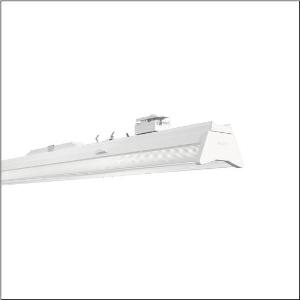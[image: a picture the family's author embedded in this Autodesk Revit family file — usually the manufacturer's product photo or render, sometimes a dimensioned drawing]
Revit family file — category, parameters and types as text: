
# Revit family: licross_r__11_performance_ho_51td16cn4exm_ed55
name_source: partatom
category: Lighting Fixtures
units: mm (PartAtom-declared; Revit-internal decimal feet)

## family parameters
Cut with Voids When Loaded = No
Host = Face
Light Source = No
Part Type = Normal
Room Calculation Point = No
Round Connector Dimension = Use Diameter
Shared = No

## types (1)
- --- (1 x LED, 14420 lm, 77.6 W, 4000K)
    Apparent Load = 78 VA
    CIE Flux Codes = 63 87 95 78 100
    Color Rendering = 80
    Color Temperature = 4000K
    Default Elevation = 1800 mm
    Description = Licross® 11 Performance HO, luminaire insert, of sheet steel, galvanised, coil coated, white, length: 1.500mm, width: 120mm, height: 123mm, LED rated luminous flux: 14.420lm, light colour: 840, control gear: ON/OFF Multilumen, CLOi, with plug, 3-pole, with phase selection, mains connection: 220..240V, AC, 50/60Hz, start of lifetime: 78W, end of service life: 87W, halogen-free wiring, primary light control with lens, of plastic, primary optical cover: cover, of PMMA, light emission: direct/indirect distribution, primary light characteristic: symmetric, protection rating (complete): IP54, insulation class (complete): insulation class I (protective earthing), certification: CE, ENEC, VDE, UKCA, protection symbol: D if used in an environment with non-conductive dust loads with corresponding accessories, impact resistance: IK06, permissible ambient temperature for indoor applications: -35..+35°C, corresponds to IFS (International Featured Standards) requirements for safety and quality in the food industry, reducing of maximum allowable ambient temperature of 5°C with ceiling mounting, LABS conformity tested according to VDMA 24364:2018-05, packaging unit: 1 piece
    Height = 114 mm
    Lamp = 1 x LED
    Lamp Light Flux = 14420 lm
    Lamp Power = 77.6 W
    Lamp count = 1
    Length = 1500 mm
    Luminous efficacy = 186 lm/W
    Manufacturer = Siteco
    ModVariant = No
    Model = 51TD16CN4EXM
    Mounting Place = Ceiling
    Mounting Type = Pendant
    Number of Poles = 1
    OnlyDefault = Yes
    Power Factor = 1
    Product Name = Licross® 11 Performance HO
    Product group = luminaire insert
    ProductGroupID = 901
    Protection Class = Protection class I
    Protection Degree = IP 54
    RLX_Detail_Level = 1
    RLX_Emergency_Light_Flux = 0 lm
    RLX_Emergency_Type = 0
    RLX_Emergency_Type_DB = No
    RlxData = <blob elided: 31901 chars, md5=4e0e2cb1>
    Socket = socket
    Standby Power = 0 W
    System Light Flux = 14420 lm
    System Power = 78 W
    Type Comments = factory setting: luminous flux: 100 % | (A | C | E) | 181 mA
    Type Image = l_1256138.jpg
    URL = http://relux.com
    VarID = @adj_055501
    Voltage = 0 V
    Weight = 0.00 kg
    Width = 120 mm

## geometry (parser evidence)
native form markers: Blend x4, Sweep x13
no freeform markers — native parametric forms only
